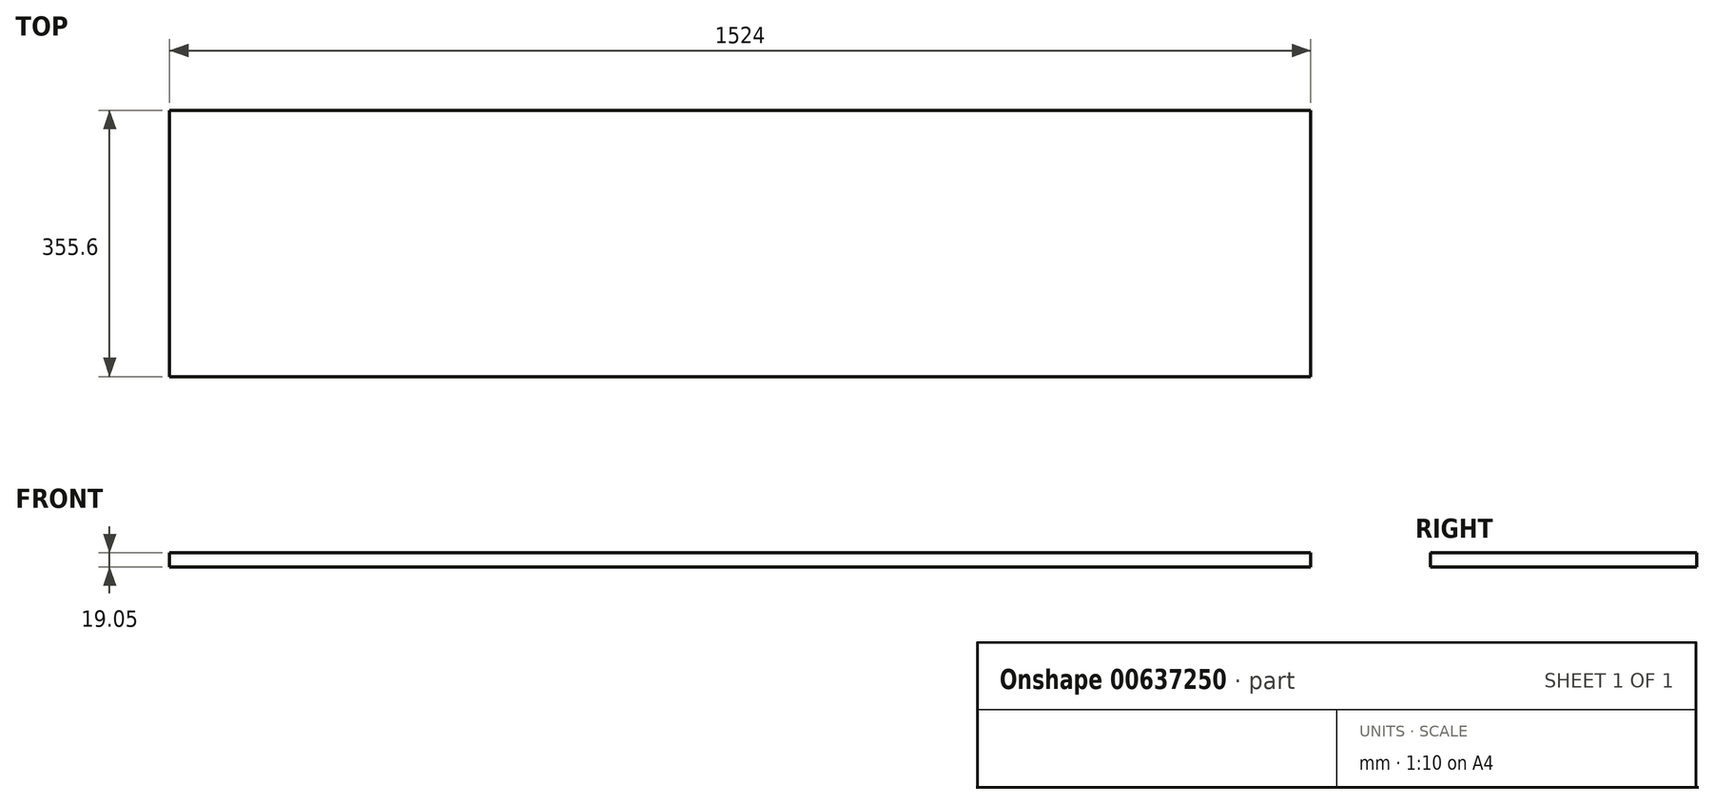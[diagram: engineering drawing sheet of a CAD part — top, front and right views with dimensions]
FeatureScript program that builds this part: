
annotation { "Feature Type Name" : "Feature", "Feature Type Description" : "" }
export const myFeature = defineFeature(function(context is Context, id is Id, definition is map)
    precondition{}
    {
        {
            var Q0;
            Q0=qCreatedBy(makeId("Top.planeOp"),FACE);
            var sketch = newSketch(context, id + "F0", { "sketchPlane" : qUnion([Q0])});
            skLineSegment(sketch, "E0.bottom", {"start": v(762, 177.8) * mm, "end": v(-762, 177.8) * mm});
            skLineSegment(sketch, "E0.top", {"start": v(762, -177.8) * mm, "end": v(-762, -177.8) * mm});
            skLineSegment(sketch, "E0.left", {"start": v(762, 177.8) * mm, "end": v(762, -177.8) * mm});
            skLineSegment(sketch, "E0.right", {"start": v(-762, 177.8) * mm, "end": v(-762, -177.8) * mm});
            skPoint(sketch, "E0.middle", {"position": v(0, 0) * mm});
            skSolve(sketch);
        }
        {
            var Q0;
            Q0=makeQuery(id+"F0.imprint","IMPRINT",FACE,{"disambiguationData":[TD([[makeQuery(id+"F0.imprint","IMPRINT",EDGE,{"derivedFrom":sQuery(id+"F0.wireOp",EDGE,"E0.bottom")}),1.0]])]});
            extrude(context, id + "F1", {"entities" : qUnion([Q0]), "depth" : 19.05 * mm, "offsetDistance" : 25.4 * mm});
        }
    });
